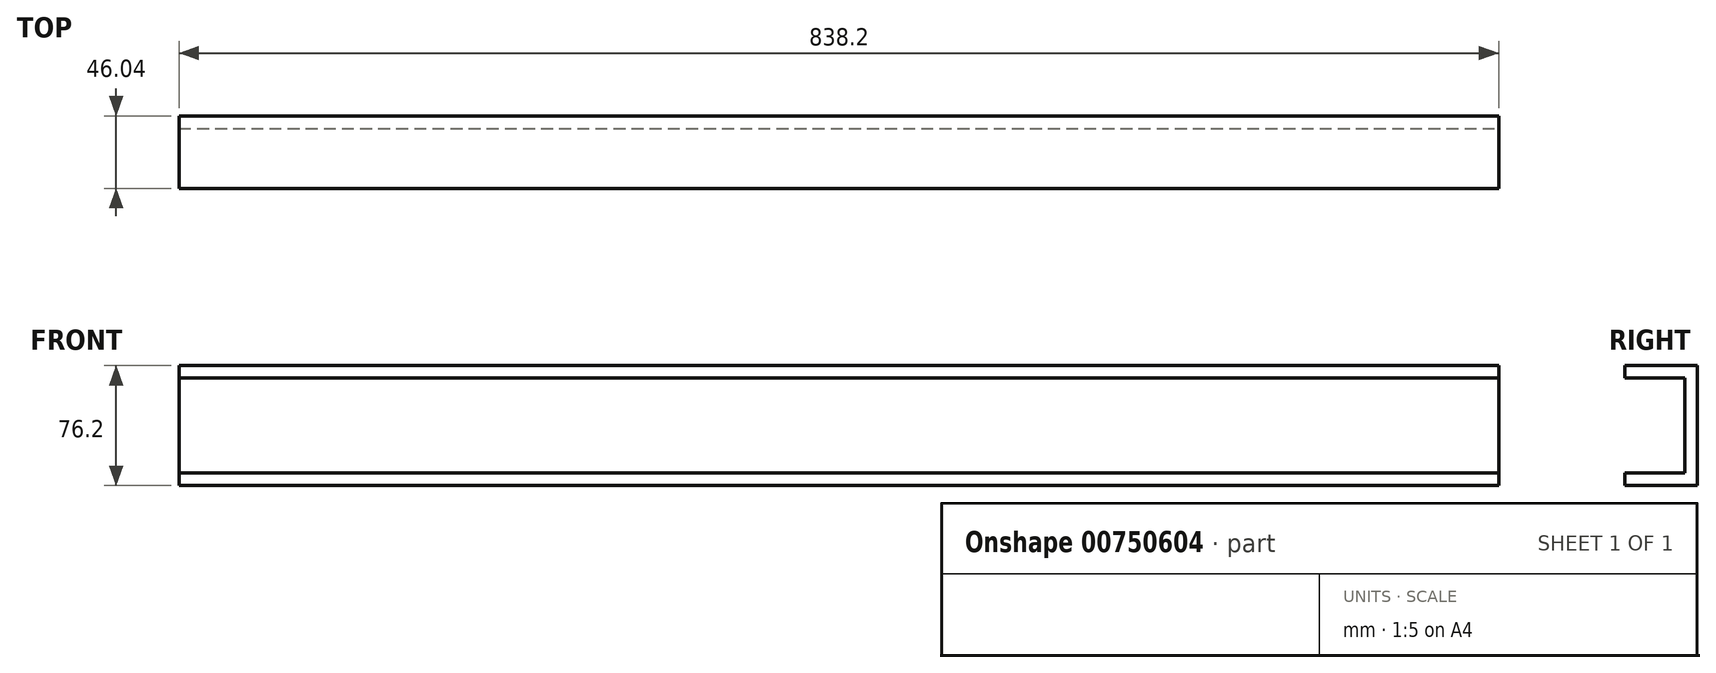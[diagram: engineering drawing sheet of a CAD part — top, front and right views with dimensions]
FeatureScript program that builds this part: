
annotation { "Feature Type Name" : "Feature", "Feature Type Description" : "" }
export const myFeature = defineFeature(function(context is Context, id is Id, definition is map)
    precondition{}
    {
        {
            var Q0;
            Q0=qCreatedBy(makeId("Front.planeOp"),FACE);
            var sketch = newSketch(context, id + "F0", { "sketchPlane" : qUnion([Q0])});
            skLineSegment(sketch, "E0", {"start": v(0, 0) * mm, "end": v(838.2, 0) * mm});
            skLineSegment(sketch, "E1", {"start": v(838.2, 0) * mm, "end": v(838.2, 76.2) * mm});
            skLineSegment(sketch, "E2", {"start": v(838.2, 76.2) * mm, "end": v(0, 76.2) * mm});
            skLineSegment(sketch, "E3", {"start": v(0, 76.2) * mm, "end": v(0, 0) * mm});
            skSolve(sketch);
        }
        {
            var Q0;
            Q0=qSketchRegion(id+"F0",true);
            extrude(context, id + "F1", {"entities" : qUnion([Q0]), "oppositeDirection" : true, "depth" : 7.94 * mm, "offsetDistance" : 25.4 * mm});
        }
        {
            var Q0;
            Q0=qCreatedBy(makeId("Front.planeOp"),FACE);
            var sketch = newSketch(context, id + "F2", { "sketchPlane" : qUnion([Q0])});
            skLineSegment(sketch, "E4.0", {"start": v(838.2, 68.26) * mm, "end": v(0, 68.26) * mm});
            skLineSegment(sketch, "E4.2", {"start": v(0, 7.94) * mm, "end": v(838.2, 7.94) * mm});
            skLineSegment(sketch, "E5.0", {"start": v(838.2, 76.2) * mm, "end": v(0, 76.2) * mm});
            skLineSegment(sketch, "E6.0", {"start": v(0, 0) * mm, "end": v(838.2, 0) * mm});
            skLineSegment(sketch, "E7", {"start": v(0, 76.2) * mm, "end": v(0, 68.26) * mm});
            skLineSegment(sketch, "E8", {"start": v(0, 7.94) * mm, "end": v(0, 0) * mm});
            skLineSegment(sketch, "E9", {"start": v(838.2, 76.2) * mm, "end": v(838.2, 68.26) * mm});
            skLineSegment(sketch, "E10", {"start": v(838.2, 0) * mm, "end": v(838.2, 7.94) * mm});
            skSolve(sketch);
        }
        {
            var Q0;
            Q0=qSketchRegion(id+"F2",true);
            extrude(context, id + "F3", {"entities" : qUnion([Q0]), "operationType" : NewBodyOperationType.ADD, "depth" : 38.1 * mm, "offsetDistance" : 25.4 * mm});
        }
    });
